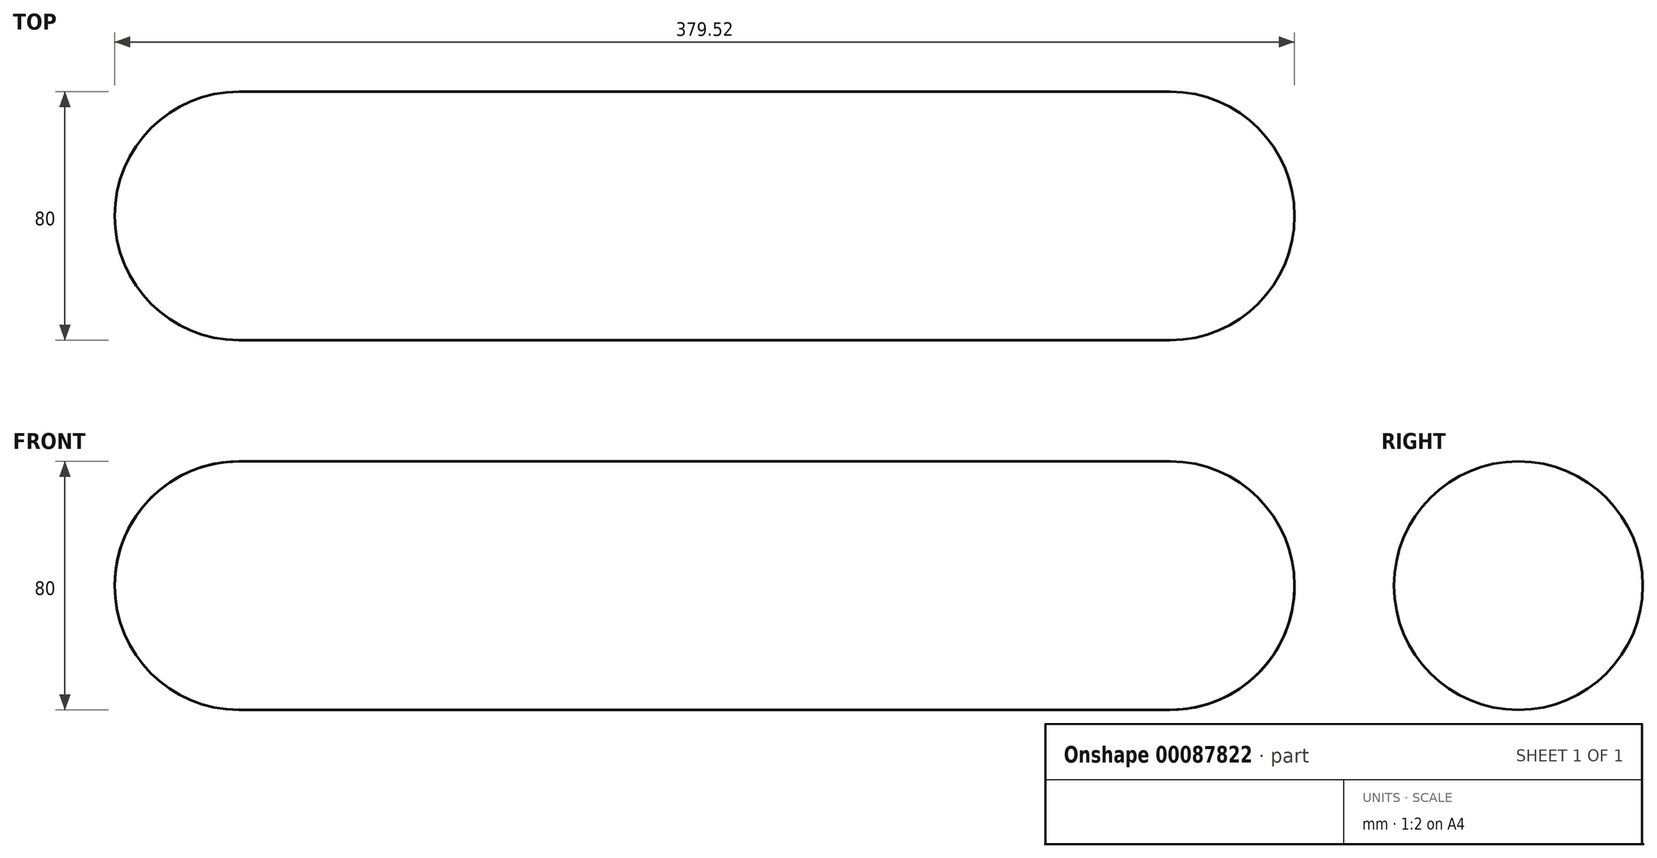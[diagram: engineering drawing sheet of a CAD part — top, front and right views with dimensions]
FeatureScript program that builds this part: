
annotation { "Feature Type Name" : "Feature", "Feature Type Description" : "" }
export const myFeature = defineFeature(function(context is Context, id is Id, definition is map)
    precondition{}
    {
        {
            var Q0;
            Q0=qCreatedBy(makeId("Front.planeOp"),FACE);
            var sketch = newSketch(context, id + "F0", { "sketchPlane" : qUnion([Q0])});
            skLineSegment(sketch, "E0", {"start": v(-149.76, 0) * mm, "end": v(149.76, 0) * mm});
            skLineSegment(sketch, "E1", {"start": v(0, 139.02) * mm, "end": v(0, -124.29) * mm, "construction": true});
            skArc(sketch, "E2.0.startCap", {"start": v(-149.76, -40) * mm, "mid": v(-178.04, -28.28) * mm, "end": v(-189.76, 0) * mm});
            skArc(sketch, "E2.0.endCap", {"start": v(189.76, 0) * mm, "mid": v(178.04, -28.28) * mm, "end": v(149.76, -40) * mm});
            skLineSegment(sketch, "E2.0.right", {"start": v(-149.76, -40) * mm, "end": v(149.76, -40) * mm});
            skLineSegment(sketch, "E3", {"start": v(-212.1, 0) * mm, "end": v(-149.76, 0) * mm});
            skPoint(sketch, "E3.startSnap0", {"position": v(-189.76, 0) * mm});
            skLineSegment(sketch, "E4", {"start": v(203.68, 0) * mm, "end": v(149.76, 0) * mm});
            skSolve(sketch);
        }
        {
            var Q0;
            Q0 = qSketchRegion(id + "F0", true);
            var Q1;
            Q1=sQuery(id+"F0.wireOp",EDGE,"E3");
            revolve(context, id + "F1", {"entities" : qUnion([Q0]), "axis" : qUnion([Q1]), "revolveType" : RevolveType.FULL});
        }
    });
